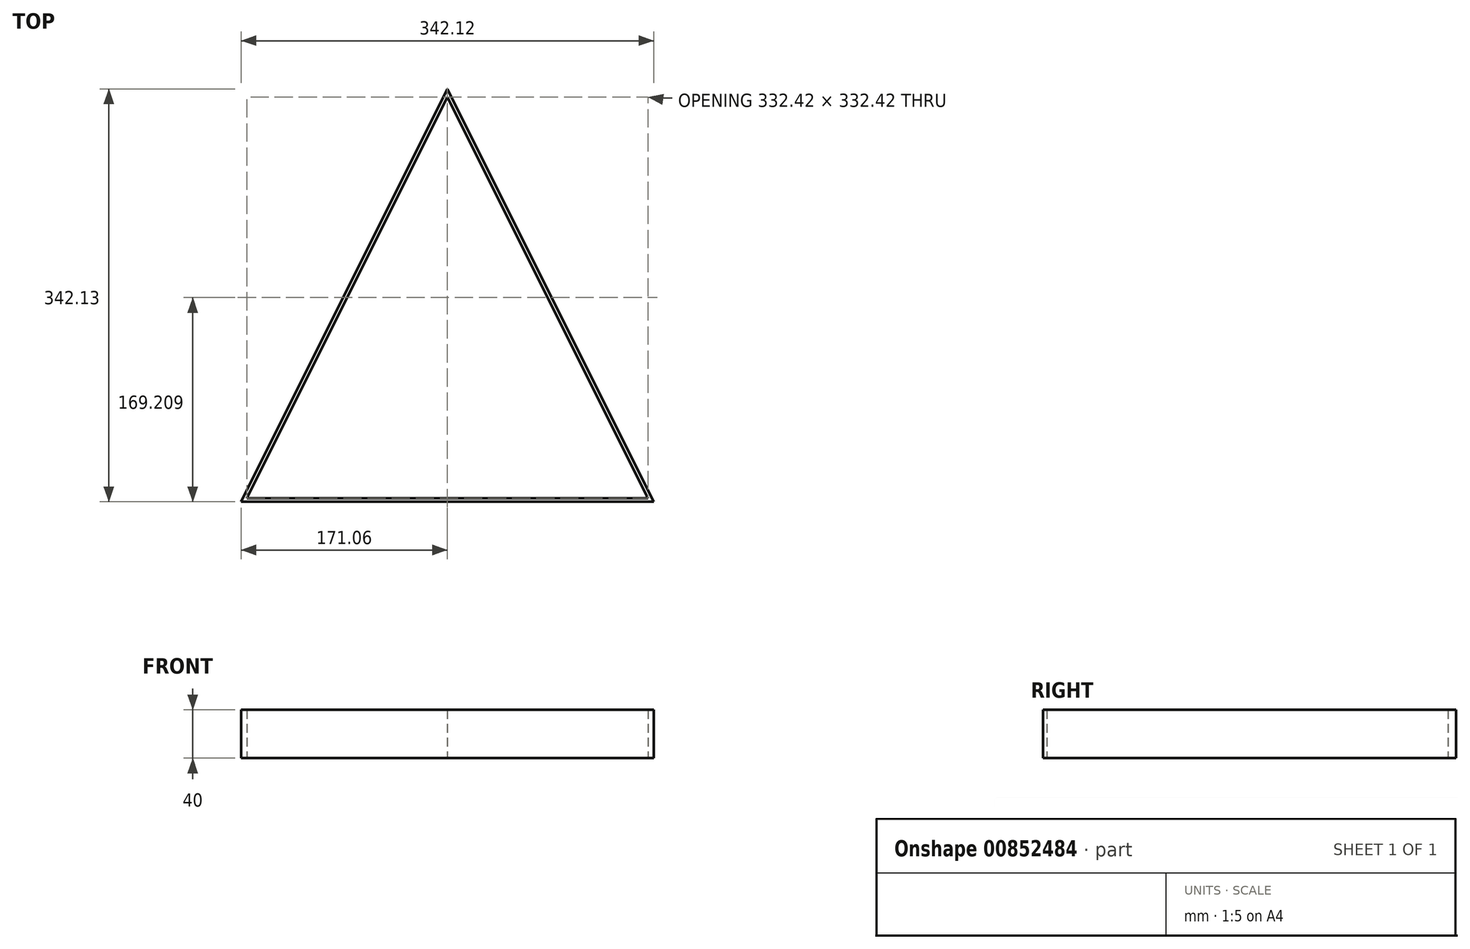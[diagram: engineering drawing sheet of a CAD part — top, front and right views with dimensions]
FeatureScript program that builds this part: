
annotation { "Feature Type Name" : "Feature", "Feature Type Description" : "" }
export const myFeature = defineFeature(function(context is Context, id is Id, definition is map)
    precondition{}
    {
        {
            var Q0;
            Q0=qCreatedBy(makeId("Top.planeOp"),FACE);
            var sketch = newSketch(context, id + "F0", { "sketchPlane" : qUnion([Q0])});
            skLineSegment(sketch, "E0", {"start": v(0, 0) * mm, "end": v(0, 342.13) * mm, "construction": true});
            skLineSegment(sketch, "E1.bottom", {"start": v(171.06, 0) * mm, "end": v(-171.06, 0) * mm, "construction": true});
            skLineSegment(sketch, "E1.top", {"start": v(171.06, 0) * mm, "end": v(-171.06, 0) * mm});
            skLineSegment(sketch, "E1.left", {"start": v(171.06, 0) * mm, "end": v(171.06, 0) * mm});
            skLineSegment(sketch, "E1.right", {"start": v(-171.06, 0) * mm, "end": v(-171.06, 0) * mm});
            skPoint(sketch, "E1.middle", {"position": v(0, 0) * mm});
            skLineSegment(sketch, "E2", {"start": v(0, 342.13) * mm, "end": v(171.06, 0) * mm});
            skLineSegment(sketch, "E3", {"start": v(-171.06, 0) * mm, "end": v(0, 342.13) * mm});
            skLineSegment(sketch, "E4", {"start": v(0, 335.42) * mm, "end": v(166.2, 3) * mm});
            skLineSegment(sketch, "E5", {"start": v(166.2, 3) * mm, "end": v(-166.2, 3) * mm});
            skLineSegment(sketch, "E6", {"start": v(-166.2, 3) * mm, "end": v(0, 335.42) * mm});
            skSolve(sketch);
        }
        {
            var Q0;
            Q0=qSketchRegion(id+"F0",true);
            extrude(context, id + "F1", {"entities" : qUnion([Q0]), "depth" : 40 * mm, "offsetDistance" : 25 * mm});
        }
    });
